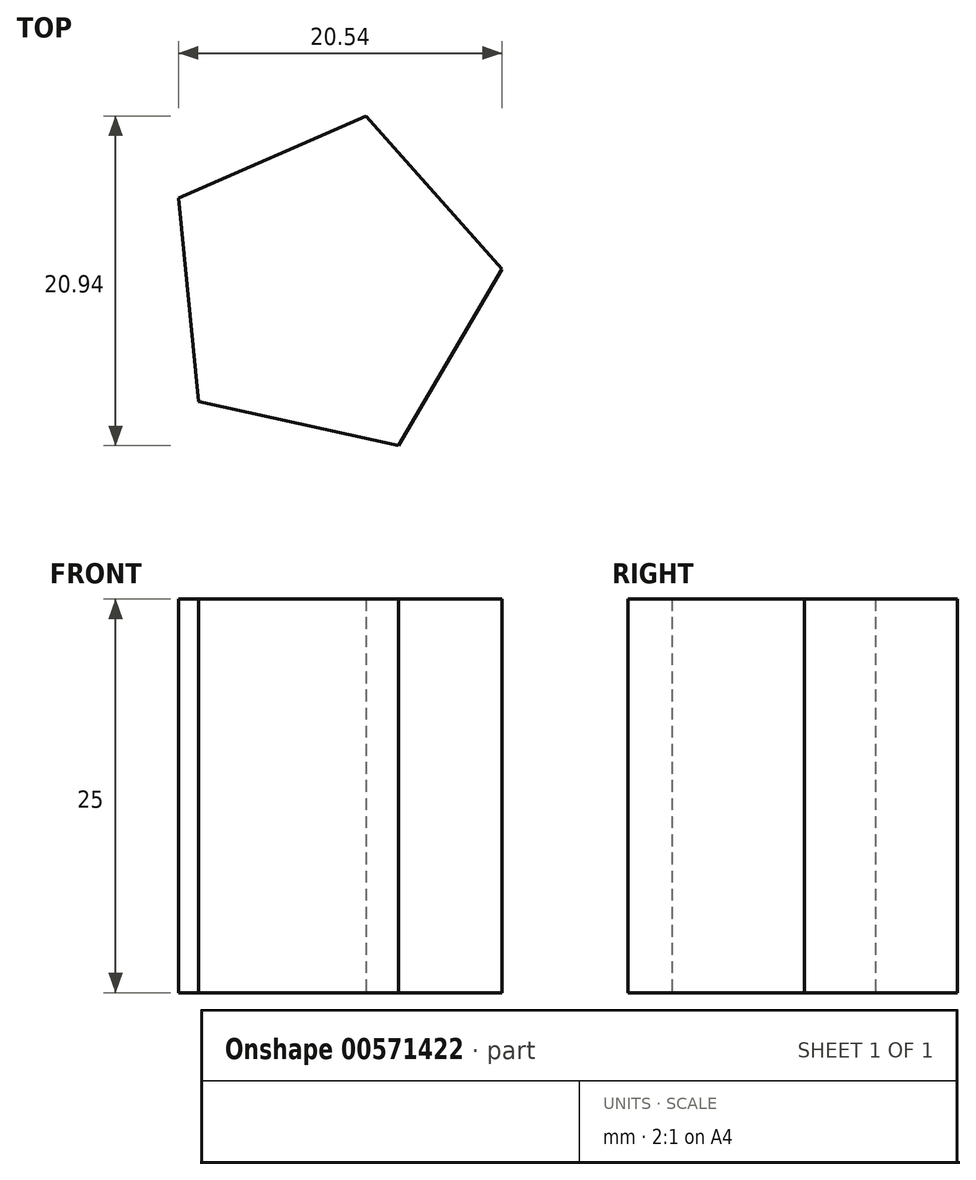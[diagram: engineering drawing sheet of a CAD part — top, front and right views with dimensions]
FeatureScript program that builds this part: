
annotation { "Feature Type Name" : "Feature", "Feature Type Description" : "" }
export const myFeature = defineFeature(function(context is Context, id is Id, definition is map)
    precondition{}
    {
        {
            var Q0;
            Q0=qCreatedBy(makeId("Top.planeOp"),FACE);
            var sketch = newSketch(context, id + "F0", { "sketchPlane" : qUnion([Q0])});
            skLineSegment(sketch, "E0.bottom", {"start": v(-53.05, 42.9) * mm, "end": v(-37.05, 42.9) * mm});
            skLineSegment(sketch, "E0.top", {"start": v(-53.05, 26.9) * mm, "end": v(-37.05, 26.9) * mm});
            skLineSegment(sketch, "E0.left", {"start": v(-53.05, 42.9) * mm, "end": v(-53.05, 26.9) * mm});
            skLineSegment(sketch, "E0.right", {"start": v(-37.05, 42.9) * mm, "end": v(-37.05, 26.9) * mm});
            skLineSegment(sketch, "E1", {"start": v(-54.74, 9.65) * mm, "end": v(-34.24, 9.65) * mm});
            skLineSegment(sketch, "E2", {"start": v(-34.24, 9.65) * mm, "end": v(-44.49, -8.1) * mm});
            skLineSegment(sketch, "E3", {"start": v(-44.49, -8.1) * mm, "end": v(-54.74, 9.65) * mm});
            skLineSegment(sketch, "E4", {"start": v(36.71, -29.06) * mm, "end": v(51.92, -34.03) * mm});
            skLineSegment(sketch, "E5", {"start": v(36.71, -29.06) * mm, "end": v(50.6, -21.1) * mm});
            skLineSegment(sketch, "E6", {"start": v(50.6, -21.1) * mm, "end": v(54.98, -27.18) * mm});
            skLineSegment(sketch, "E7", {"start": v(54.98, -27.18) * mm, "end": v(51.92, -34.03) * mm});
            skLineSegment(sketch, "E8", {"start": v(51.92, -34.03) * mm, "end": v(50.6, -21.1) * mm});
            skLineSegment(sketch, "E9", {"start": v(25.98, -42.7) * mm, "end": v(32.48, -57.32) * mm});
            skLineSegment(sketch, "E10", {"start": v(41.18, -47.67) * mm, "end": v(39.6, -55) * mm});
            skLineSegment(sketch, "E11", {"start": v(39.6, -55) * mm, "end": v(32.48, -57.32) * mm});
            skLineSegment(sketch, "E12", {"start": v(32.48, -57.32) * mm, "end": v(41.18, -47.67) * mm});
            skLineSegment(sketch, "E13", {"start": v(25.98, -42.7) * mm, "end": v(41.18, -47.67) * mm});
            skCircle(sketch, "E14.cCircle", {"center": v(33.12, 34.76) * mm, "radius": 8.95 * mm, "construction": true});
            skLineSegment(sketch, "E14.0", {"start": v(44.12, 35.83) * mm, "end": v(37.55, 24.62) * mm});
            skLineSegment(sketch, "E14.1", {"start": v(37.55, 24.62) * mm, "end": v(24.85, 27.41) * mm});
            skLineSegment(sketch, "E14.2", {"start": v(24.85, 27.41) * mm, "end": v(23.58, 40.35) * mm});
            skLineSegment(sketch, "E14.3", {"start": v(23.58, 40.35) * mm, "end": v(35.5, 45.56) * mm});
            skLineSegment(sketch, "E14.4", {"start": v(35.5, 45.56) * mm, "end": v(44.12, 35.83) * mm});
            skPoint(sketch, "E14.0.midPoint", {"position": v(40.83, 30.23) * mm});
            skSolve(sketch);
        }
        {
            var Q0;
            Q0=makeQuery(id+"F0.imprint","IMPRINT",FACE,{"disambiguationData":[TD([[makeQuery(id+"F0.imprint","IMPRINT",EDGE,{"derivedFrom":sQuery(id+"F0.wireOp",EDGE,"E14.0")}),-1.0]])]});
            extrude(context, id + "F1", {"entities" : qUnion([Q0]), "depth" : 25 * mm, "offsetDistance" : 25 * mm});
        }
    });
